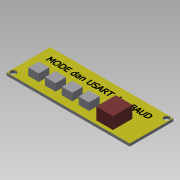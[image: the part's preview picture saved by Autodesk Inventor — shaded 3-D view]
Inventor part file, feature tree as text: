
AUTODESK INVENTOR PART (.ipt)
format: ipt  version: 2015 SP1 (Build 190203100, 203)  size: 141,312 bytes
history: native  units: mm
features: extrude x3, sketch x2
ambient origin geometry x8: Origin, YZ Plane, XZ Plane, XY Plane, X Axis, Y Axis, Z Axis, Center Point
bodies: Solid1 (feature_tree)
feature tree (5):
  sketch  "Sketch1"  dims[d0=73.55mm d1=26.14mm]
  extrude  "Extrusion1"  Depth=26.14mm
  extrude  "Extrusion2"  Depth=2.0mm
  extrude  "Extrusion3"  Depth=2.0mm
  sketch  "Sketch2"  dims[d2=3.5mm d3=2.0mm d4=2.0mm d5=3.5mm d6=2.0mm d7=2.0mm d8=10.0mm d9=11.68mm d10=12.0mm d11=2.0mm d12=6.26mm d13=6.26mm d14=6.26mm d15=6.26mm d16=10.0mm d17=6.26mm d18=6.26mm d19=10.0mm d20=6.26mm d21=6.26mm d22=10.0mm d23=6.984546mm d24=1.6mm d25=0.0mm d26=8.76mm d27=0.0mm d28=6.0mm d29=0.0mm]
